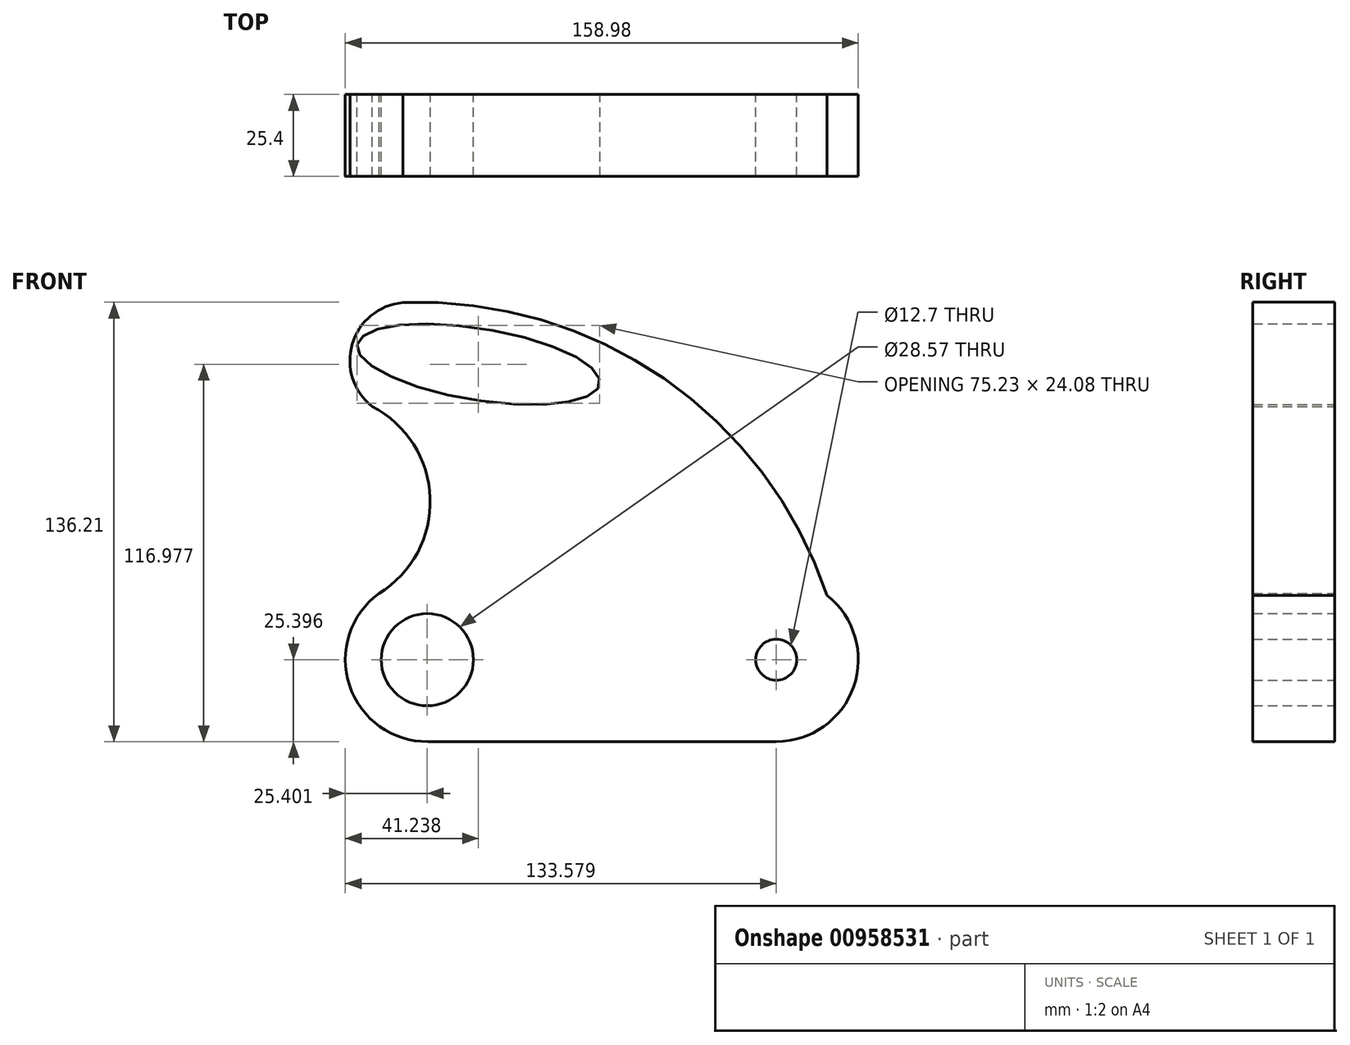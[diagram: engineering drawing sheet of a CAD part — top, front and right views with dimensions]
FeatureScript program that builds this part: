
annotation { "Feature Type Name" : "Feature", "Feature Type Description" : "" }
export const myFeature = defineFeature(function(context is Context, id is Id, definition is map)
    precondition{}
    {
        {
            var Q0;
            Q0=qCreatedBy(makeId("Front.planeOp"),FACE);
            var sketch = newSketch(context, id + "F0", { "sketchPlane" : qUnion([Q0])});
            skCircle(sketch, "E0", {"center": v(-54.09, -49.88) * mm, "radius": 25.4 * mm});
            skCircle(sketch, "E1", {"center": v(-54.09, -49.88) * mm, "radius": 14.29 * mm});
            skCircle(sketch, "E2.MirrorC", {"center": v(54.09, -49.88) * mm, "radius": 25.4 * mm});
            skCircle(sketch, "E3", {"center": v(54.09, -49.88) * mm, "radius": 6.35 * mm});
            skLineSegment(sketch, "E4", {"start": v(-53.86, -75.28) * mm, "end": v(54.09, -75.28) * mm});
            skArc(sketch, "E5", {"start": v(-69.05, -29.35) * mm, "mid": v(-53.2, 0.26) * mm, "end": v(-71.16, 28.64) * mm});
            skArc(sketch, "E6", {"start": v(-61.7, 60.84) * mm, "mid": v(-77.35, 47.95) * mm, "end": v(-71.16, 28.64) * mm});
            skArc(sketch, "E7", {"start": v(69.87, -29.98) * mm, "mid": v(19.2, 37.33) * mm, "end": v(-61.7, 60.84) * mm});
            skArc(sketch, "E8", {"start": v(-15.74, 17.24) * mm, "mid": v(-42.42, 27.95) * mm, "end": v(-71.16, 28.64) * mm});
            skArc(sketch, "E9", {"start": v(-15.74, 17.24) * mm, "mid": v(1.7, 27.65) * mm, "end": v(0.85, 47.95) * mm});
            skPoint(sketch, "E9.endSnap0", {"position": v(-77.35, 47.95) * mm});
            skEllipse(sketch, "E10", {"center": v(-38.25, 41.7) * mm, "majorRadius": 11.11 * mm, "minorRadius": 38.1 * mm, "majorAxis": v(0.16, 0.99)});
            skSolve(sketch);
        }
        {
            var Q0;
            {var subQ2=sQuery(id+"F0.wireOp",EDGE,"E6");Q0=makeQuery(id+"F0.imprint","IMPRINT",FACE,{"disambiguationData":[TD([[makeQuery(id+"F0.imprint","IMPRINT",EDGE,{"derivedFrom":subQ2}),1.0]])]});}
            var Q1;
            {var subQ4=sQuery(id+"F0.wireOp",EDGE,"E4");Q1=makeQuery(id+"F0.imprint","IMPRINT",FACE,{"disambiguationData":[TD([[makeQuery(id+"F0.imprint","IMPRINT",EDGE,{"derivedFrom":subQ4}),1.0]])]});}
            var Q2;
            Q2=makeQuery(id+"F0.imprint","IMPRINT",FACE,{"disambiguationData":[TD([[makeQuery(id+"F0.imprint","IMPRINT",EDGE,{"derivedFrom":sQuery(id+"F0.wireOp",EDGE,"E1")}),-1.0]])]});
            var Q3;
            Q3=makeQuery(id+"F0.imprint","IMPRINT",FACE,{"disambiguationData":[TD([[makeQuery(id+"F0.imprint","IMPRINT",EDGE,{"derivedFrom":sQuery(id+"F0.wireOp",EDGE,"E3")}),-1.0]])]});
            extrude(context, id + "F1", {"entities" : qUnion([Q0, Q1, Q2, Q3]), "depth" : 25.4 * mm, "offsetDistance" : 25.4 * mm});
        }
    });
